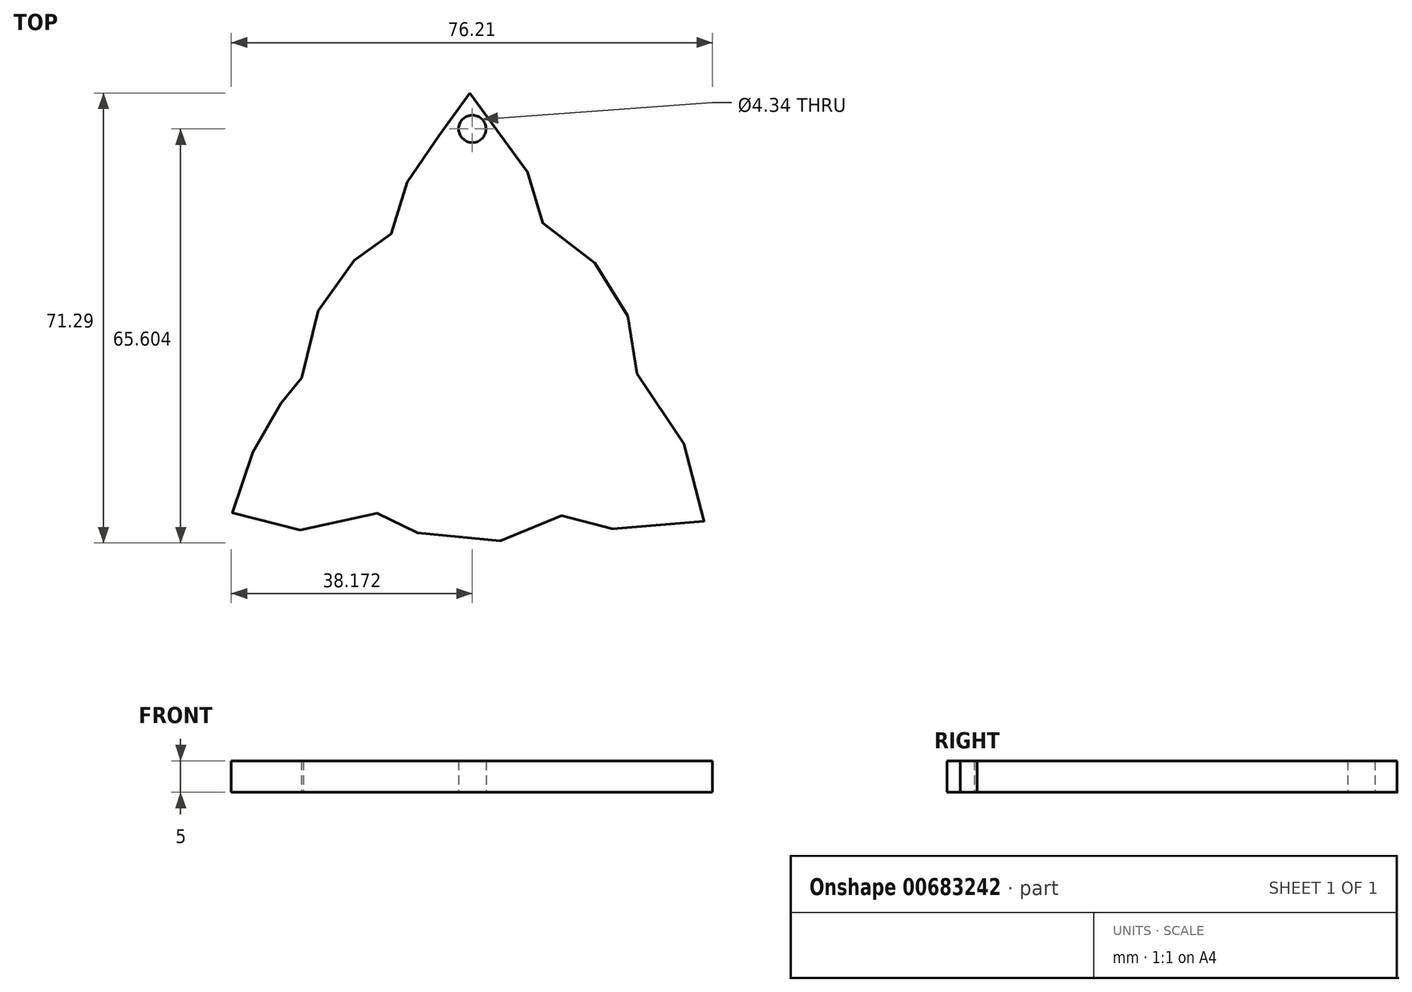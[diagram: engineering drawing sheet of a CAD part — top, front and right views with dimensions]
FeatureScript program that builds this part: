
annotation { "Feature Type Name" : "Feature", "Feature Type Description" : "" }
export const myFeature = defineFeature(function(context is Context, id is Id, definition is map)
    precondition{}
    {
        {
            var Q0;
            Q0=qCreatedBy(makeId("Top.planeOp"),FACE);
            var sketch = newSketch(context, id + "F0", { "sketchPlane" : qUnion([Q0])});
            skFitSpline(sketch, "E0", {"points": [v(40.18, 73.38) * mm, v(37.15, 70.14) * mm, v(35.2, 66.46) * mm, v(33.05, 63.44) * mm, v(29.38, 56.96) * mm, v(28.51, 51.56) * mm, v(27, 50.92) * mm, v(23.98, 49.4) * mm, v(21.39, 46.17) * mm, v(17.72, 41.41) * mm, v(14.48, 34.5) * mm, v(13.61, 27.8) * mm, v(13.83, 26.73) * mm, v(12.32, 25.87) * mm, v(9.3, 23.06) * mm, v(6.92, 18.96) * mm, v(4.11, 12.48) * mm, v(2.6, 6.86) * mm, v(8.86, 4.49) * mm, v(19.44, 4.92) * mm, v(26.79, 6.86) * mm, v(28.51, 5.35) * mm, v(33.05, 3.4) * mm, v(44.5, 2.33) * mm, v(53.35, 5.78) * mm, v(55.08, 6.43) * mm, v(57.67, 5.13) * mm, v(66.3, 4.27) * mm, v(78.18, 6.43) * mm, v(74.08, 17.88) * mm, v(66.95, 28.24) * mm, v(66.3, 31.05) * mm, v(65.23, 37.96) * mm, v(62.2, 43.57) * mm, v(58.1, 48.1) * mm, v(52.05, 52.21) * mm, v(50.97, 56.96) * mm, v(49.25, 61.07) * mm, v(40.18, 73.38) * mm]});
            skCircle(sketch, "E1", {"center": v(40.6, 67.71) * mm, "radius": 2.17 * mm});
            skSolve(sketch);
        }
        {
            var Q0;
            Q0 = qSketchRegion(id + "F0", true);
            extrude(context, id + "F1", {"entities" : qUnion([Q0]), "depth" : 5 * mm, "offsetDistance" : 25 * mm});
        }
        {
            var Q0;
            Q0=makeQuery(id+"F1.opExtrude","CAP_FACE",FACE,{"disambiguationData":[OSD([sQuery(id+"F0.wireOp",EDGE,"E0")])],"isStart":false});
            var sketch = newSketch(context, id + "F2", { "sketchPlane" : qUnion([Q0])});
            skFitSpline(sketch, "E2", {"points": [v(35.98, 54.32) * mm, v(37.75, 60.18) * mm, v(40.06, 63.55) * mm, v(44.68, 57.51) * mm, v(46.28, 53.78) * mm, v(40.6, 54.32) * mm, v(35.98, 54.32) * mm]});
            skCircle(sketch, "E3", {"center": v(40.27, 67.76) * mm, "radius": 2.7 * mm});
            skSolve(sketch);
        }
        {
            var Q0;
            Q0=makeQuery(id+"F2.imprint","IMPRINT",FACE,{"disambiguationData":[TD([[makeQuery(id+"F2.imprint","IMPRINT",EDGE,{"derivedFrom":sQuery(id+"F2.wireOp",EDGE,"E2")}),1.0]])]});
            var sketch = newSketch(context, id + "F3", { "sketchPlane" : qUnion([Q0])});
            skFitSpline(sketch, "E4", {"points": [v(34.02, 47.75) * mm, v(37.58, 48.28) * mm, v(43.44, 48.1) * mm, v(47.17, 47.21) * mm, v(47.7, 44.73) * mm, v(47.52, 41.53) * mm, v(46.1, 36.38) * mm, v(41.66, 37.27) * mm, v(35.44, 37.27) * mm, v(33.67, 41.7) * mm, v(34.02, 47.75) * mm]});
            skSolve(sketch);
        }
        {
            var Q0;
            Q0=makeQuery(id+"F2.imprint","IMPRINT",FACE,{"disambiguationData":[TD([[makeQuery(id+"F2.imprint","IMPRINT",EDGE,{"derivedFrom":sQuery(id+"F2.wireOp",EDGE,"E2")}),1.0]])]});
            var sketch = newSketch(context, id + "F4", { "sketchPlane" : qUnion([Q0])});
            skFitSpline(sketch, "E5", {"points": [v(21.06, 33) * mm, v(22.83, 37.98) * mm, v(27.27, 44.02) * mm, v(27.45, 39.22) * mm, v(28.52, 35.85) * mm, v(21.06, 33) * mm]});
            skSolve(sketch);
        }
        {
            var Q0;
            Q0=makeQuery(id+"F2.imprint","IMPRINT",FACE,{"disambiguationData":[TD([[makeQuery(id+"F2.imprint","IMPRINT",EDGE,{"derivedFrom":sQuery(id+"F2.wireOp",EDGE,"E2")}),1.0]])]});
            var sketch = newSketch(context, id + "F5", { "sketchPlane" : qUnion([Q0])});
            skFitSpline(sketch, "E6", {"points": [v(53.46, 43.04) * mm, v(53.46, 38.95) * mm, v(52.35, 35.42) * mm, v(54.2, 34.86) * mm, v(57, 33.74) * mm, v(59.22, 32.07) * mm, v(58.67, 36.16) * mm, v(56.8, 39.7) * mm, v(53.46, 43.04) * mm]});
            skSolve(sketch);
        }
        {
            var Q0;
            Q0=makeQuery(id+"F2.imprint","IMPRINT",FACE,{"disambiguationData":[TD([[makeQuery(id+"F2.imprint","IMPRINT",EDGE,{"derivedFrom":sQuery(id+"F2.wireOp",EDGE,"E2")}),1.0]])]});
            var sketch = newSketch(context, id + "F6", { "sketchPlane" : qUnion([Q0])});
            skFitSpline(sketch, "E7", {"points": [v(36.92, 30.96) * mm, v(44.73, 30.77) * mm, v(41.75, 26.3) * mm, v(40.64, 24.45) * mm, v(37.66, 28.35) * mm, v(36.92, 30.96) * mm]});
            skSolve(sketch);
        }
        {
            var Q0;
            Q0=makeQuery(id+"F2.imprint","IMPRINT",FACE,{"disambiguationData":[TD([[makeQuery(id+"F2.imprint","IMPRINT",EDGE,{"derivedFrom":sQuery(id+"F2.wireOp",EDGE,"E2")}),1.0]])]});
            var sketch = newSketch(context, id + "F7", { "sketchPlane" : qUnion([Q0])});
            skFitSpline(sketch, "E8", {"points": [v(51.23, 30.21) * mm, v(48.44, 24.45) * mm, v(45.47, 20.55) * mm, v(44.54, 18.87) * mm, v(48.63, 15.34) * mm, v(53.46, 13.11) * mm, v(58.85, 20.73) * mm, v(59.97, 24.82) * mm, v(55.88, 27.6) * mm, v(51.23, 30.21) * mm]});
            skSolve(sketch);
        }
        {
            var Q0;
            Q0=makeQuery(id+"F2.imprint","IMPRINT",FACE,{"disambiguationData":[TD([[makeQuery(id+"F2.imprint","IMPRINT",EDGE,{"derivedFrom":sQuery(id+"F2.wireOp",EDGE,"E2")}),1.0]])]});
            var sketch = newSketch(context, id + "F8", { "sketchPlane" : qUnion([Q0])});
            skFitSpline(sketch, "E9", {"points": [v(30.6, 29.65) * mm, v(24.47, 27.8) * mm, v(21.68, 25.38) * mm, v(27.07, 13.67) * mm, v(35.8, 19.43) * mm, v(34.87, 20.92) * mm, v(32.83, 24.45) * mm, v(30.6, 29.65) * mm]});
            skSolve(sketch);
        }
        {
            var Q0;
            Q0=makeQuery(id+"F2.imprint","IMPRINT",FACE,{"disambiguationData":[TD([[makeQuery(id+"F2.imprint","IMPRINT",EDGE,{"derivedFrom":sQuery(id+"F2.wireOp",EDGE,"E2")}),1.0]])]});
            var sketch = newSketch(context, id + "F9", { "sketchPlane" : qUnion([Q0])});
            skFitSpline(sketch, "E10", {"points": [v(34.69, 9.95) * mm, v(40.08, 15.16) * mm, v(40.82, 14.04) * mm, v(42.31, 12.92) * mm, v(47.51, 10.14) * mm, v(43.98, 9.2) * mm, v(34.69, 9.95) * mm]});
            skSolve(sketch);
        }
        {
            var Q0;
            Q0=makeQuery(id+"F2.imprint","IMPRINT",FACE,{"disambiguationData":[TD([[makeQuery(id+"F2.imprint","IMPRINT",EDGE,{"derivedFrom":sQuery(id+"F2.wireOp",EDGE,"E2")}),1.0]])]});
            var sketch = newSketch(context, id + "F10", { "sketchPlane" : qUnion([Q0])});
            skFitSpline(sketch, "E11", {"points": [v(15.17, 20.55) * mm, v(10.15, 11.07) * mm, v(20.38, 11.8) * mm, v(19.26, 13.67) * mm, v(17.59, 17.2) * mm, v(15.17, 20.55) * mm]});
            skSolve(sketch);
        }
        {
            var Q0;
            Q0=makeQuery(id+"F2.imprint","IMPRINT",FACE,{"disambiguationData":[TD([[makeQuery(id+"F2.imprint","IMPRINT",EDGE,{"derivedFrom":sQuery(id+"F2.wireOp",EDGE,"E2")}),1.0]])]});
            var sketch = newSketch(context, id + "F11", { "sketchPlane" : qUnion([Q0])});
            skFitSpline(sketch, "E12", {"points": [v(64.62, 20.36) * mm, v(63.31, 17.39) * mm, v(59.6, 11.44) * mm, v(70.38, 10.88) * mm, v(66.47, 18.87) * mm, v(64.62, 20.36) * mm]});
            skSolve(sketch);
        }
        {
            var Q0;
            Q0=sQuery(id+"F2.wireOp",EDGE,"E2");
            extrude(context, id + "F12", {"bodyType" : ToolBodyType.SURFACE, "surfaceEntities" : qUnion([Q0]), "depth" : -4 * mm, "offsetDistance" : 25 * mm});
        }
        {
            var Q0;
            Q0=sQuery(id+"F3.wireOp",EDGE,"E4");
            extrude(context, id + "F13", {"bodyType" : ToolBodyType.SURFACE, "surfaceEntities" : qUnion([Q0]), "depth" : -4 * mm, "offsetDistance" : 25 * mm});
        }
        {
            var Q0;
            Q0=sQuery(id+"F5.wireOp",EDGE,"E6");
            extrude(context, id + "F14", {"bodyType" : ToolBodyType.SURFACE, "surfaceEntities" : qUnion([Q0]), "depth" : -4 * mm, "offsetDistance" : 25 * mm});
        }
        {
            var Q0;
            Q0=sQuery(id+"F4.wireOp",EDGE,"E5");
            extrude(context, id + "F15", {"bodyType" : ToolBodyType.SURFACE, "surfaceEntities" : qUnion([Q0]), "depth" : -4 * mm, "offsetDistance" : 25 * mm});
        }
        {
            var Q0;
            Q0=sQuery(id+"F6.wireOp",EDGE,"E7");
            extrude(context, id + "F16", {"bodyType" : ToolBodyType.SURFACE, "surfaceEntities" : qUnion([Q0]), "depth" : -4 * mm, "offsetDistance" : 25 * mm});
        }
        {
            var Q0;
            Q0=sQuery(id+"F7.wireOp",EDGE,"E8");
            extrude(context, id + "F17", {"bodyType" : ToolBodyType.SURFACE, "surfaceEntities" : qUnion([Q0]), "depth" : -4 * mm, "offsetDistance" : 25 * mm});
        }
        {
            var Q0;
            Q0=sQuery(id+"F8.wireOp",EDGE,"E9");
            extrude(context, id + "F18", {"bodyType" : ToolBodyType.SURFACE, "surfaceEntities" : qUnion([Q0]), "depth" : -4 * mm, "offsetDistance" : 25 * mm});
        }
        {
            var Q0;
            Q0=sQuery(id+"F9.wireOp",EDGE,"E10");
            extrude(context, id + "F19", {"bodyType" : ToolBodyType.SURFACE, "surfaceEntities" : qUnion([Q0]), "depth" : -4 * mm, "offsetDistance" : 25 * mm});
        }
        {
            var Q0;
            Q0=sQuery(id+"F10.wireOp",EDGE,"E11");
            extrude(context, id + "F20", {"bodyType" : ToolBodyType.SURFACE, "surfaceEntities" : qUnion([Q0]), "depth" : -4 * mm, "offsetDistance" : 25 * mm});
        }
        {
            var Q0;
            Q0=sQuery(id+"F11.wireOp",EDGE,"E12");
            extrude(context, id + "F21", {"bodyType" : ToolBodyType.SURFACE, "surfaceEntities" : qUnion([Q0]), "depth" : -4 * mm, "offsetDistance" : 25 * mm});
        }
        {
            var Q0;
            Q0=makeQuery(id+"F0.imprint","IMPRINT",FACE,{"disambiguationData":[TD([[makeQuery(id+"F0.imprint","IMPRINT",EDGE,{"derivedFrom":sQuery(id+"F0.wireOp",EDGE,"E0")}),1.0]])]});
            extrude(context, id + "F22", {"entities" : qUnion([Q0]), "operationType" : NewBodyOperationType.ADD, "depth" : 1 * mm, "offsetDistance" : 25 * mm});
        }
    });
